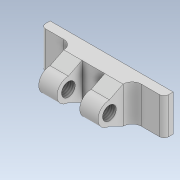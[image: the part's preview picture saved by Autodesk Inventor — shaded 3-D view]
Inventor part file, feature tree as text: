
AUTODESK INVENTOR PART (.ipt)
format: ipt  version: 2020.4 (Build 244396000, 396)  size: 164,864 bytes
history: native  units: mm
features: extrude x6, sketch x4, fillet x2, thread x1
ambient origin geometry x8: Origin, YZ Plane, XZ Plane, XY Plane, X Axis, Y Axis, Z Axis, Center Point
bodies: Solid1 (feature_tree)
feature tree (13):
  sketch  "Sketch1"  dims[d0=27.0mm d1=8.0mm]
  extrude  "Extrusion1"  Depth=8.0mm
  extrude  "Extrusion2"  Depth=13.0mm
  extrude  "Extrusion3"  Depth=4.0mm TaperAngle=0.0deg
  fillet  "Fillet1"  Radius=10.0mm
  extrude  "Extrusion4"  Depth=13.0mm
  extrude  "Extrusion5"  Depth=20.0mm TaperAngle=0.0deg
  extrude  "Extrusion6"  Depth=5.0mm
  fillet  "Fillet2"  Radius=4.0mm
  thread  "Thread1"  [1 undecoded]
  sketch  "Sketch3"  dims[d2=17.0mm d3=13.0mm]
  sketch  "Sketch5"  dims[d4=2.0mm d5=0.0mm d6=4.0mm d7=0.0mm d8=10.0mm d9=0.0mm]
  sketch  "Sketch6"  dims[d10=2.0mm d11=3.0mm d12=20.0mm d13=0.0mm d14=5.0mm d17=4.0mm d18=5.0mm d19=10.0mm d20=0.0mm d21=8.0mm d22=0.0mm d23=1.0mm d24=13.0mm d25=0.0mm]
note: 1 required parameter value undecoded (feature->parameter linkage not recoverable at this tier; creation-order binding heuristic only, values carry confidence <= 0.55)
